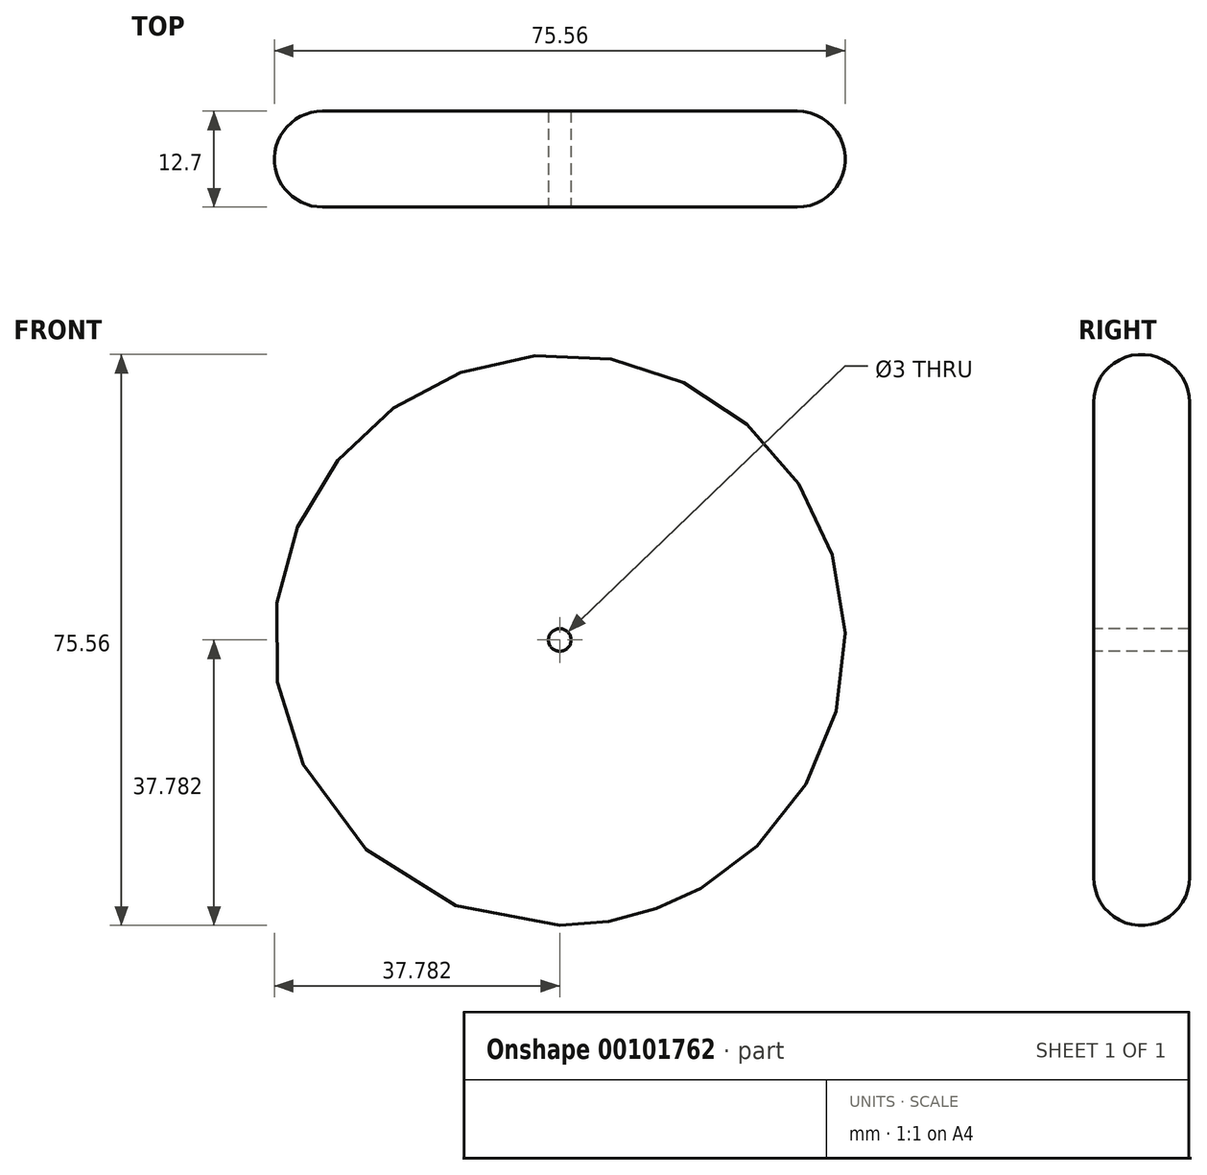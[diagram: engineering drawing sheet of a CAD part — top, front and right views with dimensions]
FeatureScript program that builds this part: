
annotation { "Feature Type Name" : "Feature", "Feature Type Description" : "" }
export const myFeature = defineFeature(function(context is Context, id is Id, definition is map)
    precondition{}
    {
        {
            var Q0;
            Q0=qCreatedBy(makeId("Front.planeOp"),FACE);
            var sketch = newSketch(context, id + "F0", { "sketchPlane" : qUnion([Q0])});
            skCircle(sketch, "E0", {"center": v(-56.97, 43.92) * mm, "radius": 37.78 * mm});
            skSolve(sketch);
        }
        {
            var Q0;
            Q0 = qSketchRegion(id + "F0", true);
            extrude(context, id + "F1", {"entities" : qUnion([Q0]), "depth" : 12.7 * mm});
        }
        {
            var Q0;
            Q0=makeQuery(id+"F1.opExtrude","CAP_EDGE",EDGE,{"disambiguationData":[OSD([sQuery(id+"F0.wireOp",EDGE,"E0")])],"isStart":false});
            fillet(context, id + "F2", {"entities" : qUnion([Q0]), "radius" : 6.35 * mm, "tangentPropagation" : true, "allowEdgeOverflow" : false});
        }
        {
            var Q0;
            Q0=makeQuery(id+"F1.opExtrude","CAP_EDGE",EDGE,{"disambiguationData":[OSD([sQuery(id+"F0.wireOp",EDGE,"E0")])],"isStart":true});
            fillet(context, id + "F3", {"entities" : qUnion([Q0]), "radius" : 6.35 * mm, "tangentPropagation" : true, "allowEdgeOverflow" : false});
        }
        {
            var Q0;
            Q0=makeQuery(id+"F1.opExtrude","CAP_FACE",FACE,{"disambiguationData":[OSD([sQuery(id+"F0.wireOp",EDGE,"E0")])],"isStart":false});
            var sketch = newSketch(context, id + "F4", { "sketchPlane" : qUnion([Q0])});
            skCircle(sketch, "E1", {"center": v(-56.97, 43.92) * mm, "radius": 1.5 * mm});
            skSolve(sketch);
        }
        {
            var Q0;
            Q0 = qSketchRegion(id + "F4", true);
            extrude(context, id + "F5", {"entities" : qUnion([Q0]), "operationType" : NewBodyOperationType.REMOVE, "endBound" : BoundingType.THROUGH_ALL, "oppositeDirection" : true, "depth" : 25.4 * mm});
        }
    });
